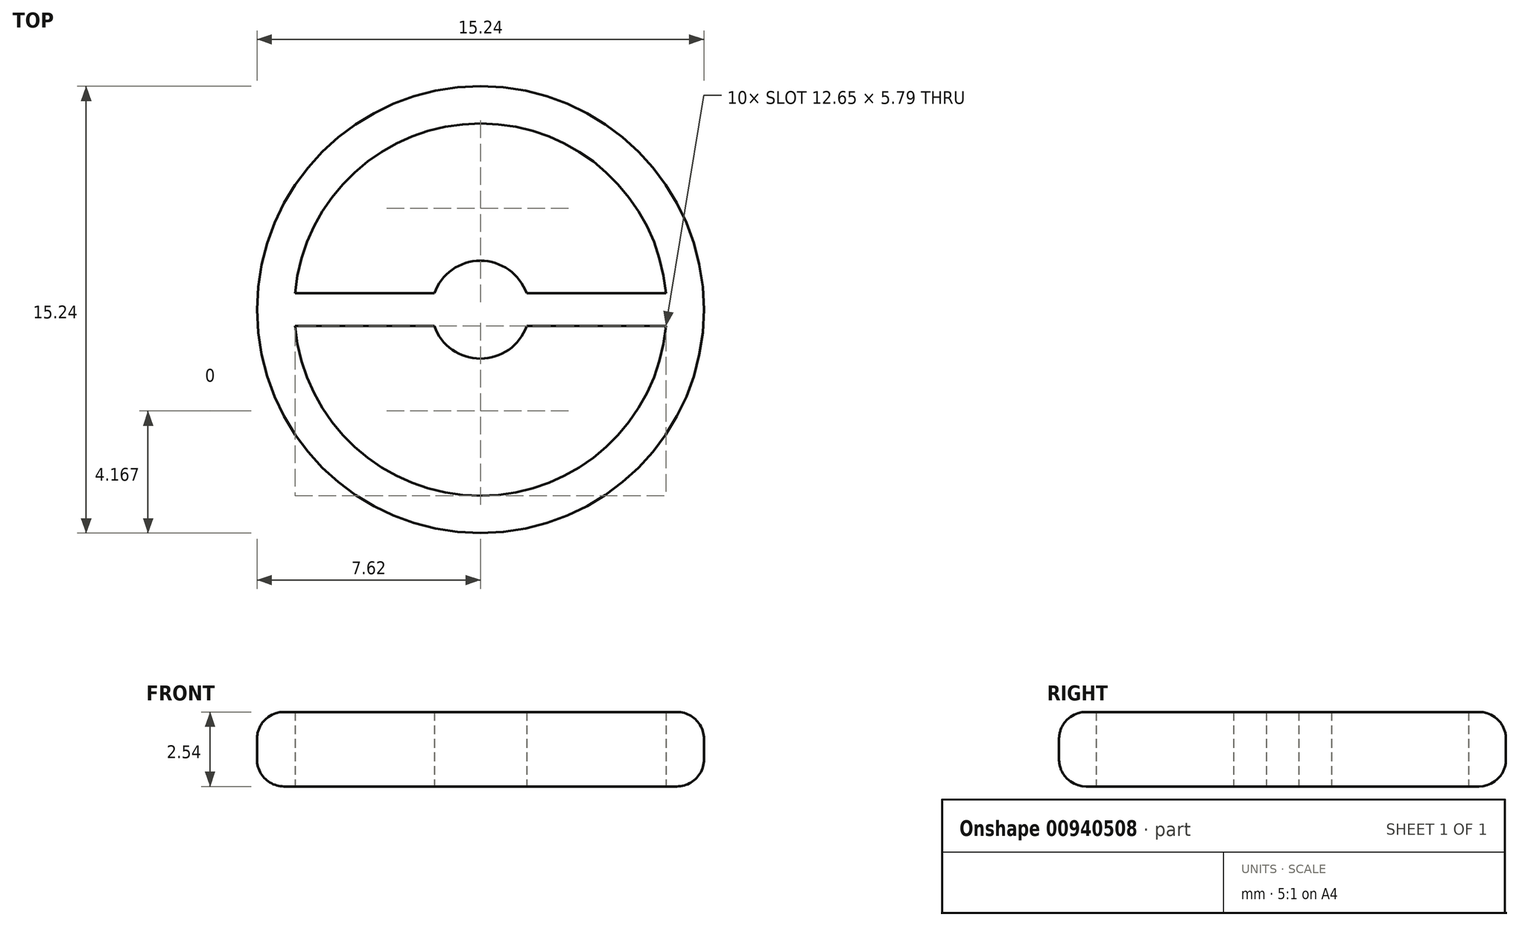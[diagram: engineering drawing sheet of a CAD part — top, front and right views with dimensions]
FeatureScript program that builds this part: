
annotation { "Feature Type Name" : "Feature", "Feature Type Description" : "" }
export const myFeature = defineFeature(function(context is Context, id is Id, definition is map)
    precondition{}
    {
        {
            var Q0;
            Q0=qCreatedBy(makeId("Top.planeOp"),FACE);
            var sketch = newSketch(context, id + "F0", { "sketchPlane" : qUnion([Q0])});
            skArc(sketch, "E0", {"start": v(-6.35, 0) * mm, "mid": v(-4.5, -4.5) * mm, "end": v(0, -6.35) * mm});
            skLineSegment(sketch, "E1", {"start": v(0, 0) * mm, "end": v(0, 6.35) * mm});
            skLineSegment(sketch, "E2", {"start": v(0, 6.35) * mm, "end": v(0, -6.35) * mm});
            skLineSegment(sketch, "E3", {"start": v(0, -6.35) * mm, "end": v(0, 0) * mm});
            skArc(sketch, "E4.trimOffspring", {"start": v(6.35, 0) * mm, "mid": v(4.5, 4.5) * mm, "end": v(0, 6.35) * mm});
            skArc(sketch, "E5.MirrorCS", {"start": v(6.35, 0) * mm, "mid": v(4.5, -4.5) * mm, "end": v(0, -6.35) * mm});
            skArc(sketch, "E6.MirrorCS", {"start": v(-6.35, 0) * mm, "mid": v(-4.5, 4.5) * mm, "end": v(0, 6.35) * mm});
            skCircle(sketch, "E7", {"center": v(0, 0) * mm, "radius": 7.62 * mm});
            skLineSegment(sketch, "E8", {"start": v(0, 0) * mm, "end": v(6.35, 0) * mm});
            skLineSegment(sketch, "E9", {"start": v(-6.35, 0) * mm, "end": v(0, 0) * mm});
            skLineSegment(sketch, "E10", {"start": v(0, 0) * mm, "end": v(0, 0.56) * mm});
            skLineSegment(sketch, "E11", {"start": v(0, 0.56) * mm, "end": v(-6.33, 0.56) * mm});
            skLineSegment(sketch, "E12.MirrorCS", {"start": v(0, -0.56) * mm, "end": v(-6.33, -0.56) * mm});
            skLineSegment(sketch, "E13.MirrorCS", {"start": v(0, -0.56) * mm, "end": v(6.33, -0.56) * mm});
            skLineSegment(sketch, "E14.MirrorCS", {"start": v(6.35, 0) * mm, "end": v(0, 0) * mm});
            skLineSegment(sketch, "E15.MirrorCS", {"start": v(0, 0.56) * mm, "end": v(6.33, 0.56) * mm});
            skCircle(sketch, "E16", {"center": v(0, 0) * mm, "radius": 1.67 * mm});
            skSolve(sketch);
        }
        {
            var Q0;
            {var subQ0=sQuery(id+"F0.wireOp",EDGE,"AciXeK0I-HK34-pKsL-Z3A6-GTDgTVSjJ2Cx");Q0=makeQuery(id+"F0.imprint","IMPRINT",FACE,{"disambiguationData":[TD([[makeQuery(id+"F0.imprint","IMPRINT",EDGE,{"derivedFrom":subQ0}),-1.0]])]});}
            var Q1;
            {var subQ0=sQuery(id+"F0.wireOp",EDGE,"AciXeK0I-HK34-pKsL-Z3A6-GTDgTVSjJ2Cx");Q1=makeQuery(id+"F0.imprint","IMPRINT",FACE,{"disambiguationData":[TD([[makeQuery(id+"F0.imprint","IMPRINT",EDGE,{"derivedFrom":subQ0}),1.0]])]});}
            var Q2;
            {var subQ0=sQuery(id+"F0.wireOp",EDGE,"cbf63e7e-f145-47e9-b27e-1f5866966e060.MirrorCS");Q2=makeQuery(id+"F0.imprint","IMPRINT",FACE,{"disambiguationData":[TD([[makeQuery(id+"F0.imprint","IMPRINT",EDGE,{"derivedFrom":subQ0}),1.0]])]});}
            var Q3;
            {var subQ0=sQuery(id+"F0.wireOp",EDGE,"33b9d93b-3f5e-4f86-a8ca-2ba8e78154330.MirrorCS");Q3=makeQuery(id+"F0.imprint","IMPRINT",FACE,{"disambiguationData":[TD([[makeQuery(id+"F0.imprint","IMPRINT",EDGE,{"derivedFrom":subQ0}),1.0]])]});}
            var Q4;
            {var subQ0=sQuery(id+"F0.wireOp",EDGE,"e4d35818-757a-4e43-8ab9-d806485e3f060.MirrorCS");Q4=makeQuery(id+"F0.imprint","IMPRINT",FACE,{"disambiguationData":[TD([[makeQuery(id+"F0.imprint","IMPRINT",EDGE,{"derivedFrom":subQ0}),1.0]])]});}
            var Q5;
            Q5=makeQuery(id+"F0.imprint","IMPRINT",FACE,{"disambiguationData":[TD([[makeQuery(id+"F0.imprint","IMPRINT",EDGE,{"derivedFrom":sQuery(id+"F0.wireOp",EDGE,"E7")}),1.0]])]});
            var Q6;
            {var subQ3=sQuery(id+"F0.wireOp",EDGE,"E11");var subQ5=sQuery(id+"F0.wireOp",EDGE,"E16");var subQ7=makeQuery(id+"F0.imprint","INTERSECT",VERTEX,{"derivedFrom":[subQ3,subQ5]});var subQ8=makeQuery(id+"F0.imprint","IMPRINT",EDGE,{"disambiguationData":[TD([[subQ7,-1.0]])],"derivedFrom":subQ5});Q6=qUnion([makeQuery(id+"F0.imprint","IMPRINT",FACE,{"disambiguationData":[TD([[subQ8,1.0]])]}),makeQuery(id+"F0.imprint","IMPRINT",FACE,{"disambiguationData":[TD([[makeQuery(id+"F0.imprint","IMPRINT",EDGE,{"disambiguationData":[TD([[subQ7,-1.0]])],"derivedFrom":subQ3}),1.0]])]})]);}
            var Q7;
            {var subQ0=sQuery(id+"F0.wireOp",EDGE,"E12.MirrorCS");var subQ5=sQuery(id+"F0.wireOp",EDGE,"E16");var subQ6=makeQuery(id+"F0.imprint","INTERSECT",VERTEX,{"derivedFrom":[subQ0,subQ5]});var subQ8=makeQuery(id+"F0.imprint","IMPRINT",EDGE,{"disambiguationData":[TD([[subQ6,1.0]])],"derivedFrom":subQ5});Q7=qUnion([makeQuery(id+"F0.imprint","IMPRINT",FACE,{"disambiguationData":[TD([[makeQuery(id+"F0.imprint","IMPRINT",EDGE,{"disambiguationData":[TD([[subQ6,-1.0]])],"derivedFrom":subQ0}),-1.0]])]}),makeQuery(id+"F0.imprint","IMPRINT",FACE,{"disambiguationData":[TD([[subQ8,1.0]])]})]);}
            var Q8;
            {var subQ3=sQuery(id+"F0.wireOp",EDGE,"E8");var subQ5=sQuery(id+"F0.wireOp",EDGE,"E16");var subQ6=makeQuery(id+"F0.imprint","INTERSECT",VERTEX,{"derivedFrom":[subQ3,subQ5]});Q8=makeQuery(id+"F0.imprint","IMPRINT",FACE,{"disambiguationData":[TD([[makeQuery(id+"F0.imprint","IMPRINT",EDGE,{"disambiguationData":[TD([[subQ6,-1.0]])],"derivedFrom":subQ5}),1.0]])]});}
            var Q9;
            {var subQ0=sQuery(id+"F0.wireOp",EDGE,"E13.MirrorCS");var subQ3=sQuery(id+"F0.wireOp",EDGE,"E8");var subQ5=sQuery(id+"F0.wireOp",EDGE,"E16");var subQ6=makeQuery(id+"F0.imprint","INTERSECT",VERTEX,{"derivedFrom":[subQ3,subQ5]});var subQ7=makeQuery(id+"F0.imprint","INTERSECT",VERTEX,{"derivedFrom":[subQ0,subQ5]});var subQ8=makeQuery(id+"F0.imprint","IMPRINT",EDGE,{"disambiguationData":[TD([[subQ6,1.0]])],"derivedFrom":subQ5});Q9=qUnion([makeQuery(id+"F0.imprint","IMPRINT",FACE,{"disambiguationData":[TD([[makeQuery(id+"F0.imprint","IMPRINT",EDGE,{"disambiguationData":[TD([[subQ7,-1.0]])],"derivedFrom":subQ0}),1.0]])]}),makeQuery(id+"F0.imprint","IMPRINT",FACE,{"disambiguationData":[TD([[subQ8,1.0]])]})]);}
            var Q10;
            {var subQ0=sQuery(id+"F0.wireOp",EDGE,"E16");var subQ1=sQuery(id+"F0.wireOp",EDGE,"E1");var subQ2=makeQuery(id+"F0.imprint","INTERSECT",VERTEX,{"derivedFrom":[subQ1,subQ0]});Q10=makeQuery(id+"F0.imprint","IMPRINT",FACE,{"disambiguationData":[TD([[makeQuery(id+"F0.imprint","IMPRINT",EDGE,{"disambiguationData":[TD([[subQ2,1.0]])],"derivedFrom":subQ0}),1.0]])]});}
            var Q11;
            {var subQ0=sQuery(id+"F0.wireOp",EDGE,"E16");var subQ1=sQuery(id+"F0.wireOp",EDGE,"E1");var subQ2=makeQuery(id+"F0.imprint","INTERSECT",VERTEX,{"derivedFrom":[subQ1,subQ0]});Q11=makeQuery(id+"F0.imprint","IMPRINT",FACE,{"disambiguationData":[TD([[makeQuery(id+"F0.imprint","IMPRINT",EDGE,{"disambiguationData":[TD([[subQ2,-1.0]])],"derivedFrom":subQ0}),1.0]])]});}
            var Q12;
            {var subQ0=sQuery(id+"F0.wireOp",EDGE,"E16");var subQ1=sQuery(id+"F0.wireOp",EDGE,"E2");var subQ2=makeQuery(id+"F0.imprint","INTERSECT",VERTEX,{"derivedFrom":[subQ1,subQ0]});Q12=makeQuery(id+"F0.imprint","IMPRINT",FACE,{"disambiguationData":[TD([[makeQuery(id+"F0.imprint","IMPRINT",EDGE,{"disambiguationData":[TD([[subQ2,1.0]])],"derivedFrom":subQ0}),1.0]])]});}
            var Q13;
            {var subQ0=sQuery(id+"F0.wireOp",EDGE,"E16");var subQ1=sQuery(id+"F0.wireOp",EDGE,"E2");var subQ2=makeQuery(id+"F0.imprint","INTERSECT",VERTEX,{"derivedFrom":[subQ1,subQ0]});Q13=makeQuery(id+"F0.imprint","IMPRINT",FACE,{"disambiguationData":[TD([[makeQuery(id+"F0.imprint","IMPRINT",EDGE,{"disambiguationData":[TD([[subQ2,-1.0]])],"derivedFrom":subQ0}),1.0]])]});}
            var Q14;
            {var subQ3=sQuery(id+"F0.wireOp",EDGE,"E15.MirrorCS");var subQ5=sQuery(id+"F0.wireOp",EDGE,"E16");var subQ7=makeQuery(id+"F0.imprint","INTERSECT",VERTEX,{"derivedFrom":[subQ3,subQ5]});Q14=makeQuery(id+"F0.imprint","IMPRINT",FACE,{"disambiguationData":[TD([[makeQuery(id+"F0.imprint","IMPRINT",EDGE,{"disambiguationData":[TD([[subQ7,-1.0]])],"derivedFrom":subQ3}),-1.0]])]});}
            extrude(context, id + "F1", {"entities" : qUnion([Q0, Q1, Q2, Q3, Q4, Q5, Q6, Q7, Q8, Q9, Q10, Q11, Q12, Q13, Q14]), "depth" : 2.54 * mm, "offsetDistance" : 25.4 * mm});
        }
        {
            var Q0;
            Q0=makeQuery(id+"F1.opExtrude","CAP_EDGE",EDGE,{"disambiguationData":[OSD([sQuery(id+"F0.wireOp",EDGE,"E7")])],"isStart":false});
            var Q1;
            Q1=makeQuery(id+"F1.opExtrude","CAP_EDGE",EDGE,{"disambiguationData":[OSD([sQuery(id+"F0.wireOp",EDGE,"E7")])],"isStart":true});
            fillet(context, id + "F2", {"entities" : qUnion([Q0, Q1]), "radius" : 0.92 * mm, "tangentPropagation" : true, "allowEdgeOverflow" : false});
        }
    });
